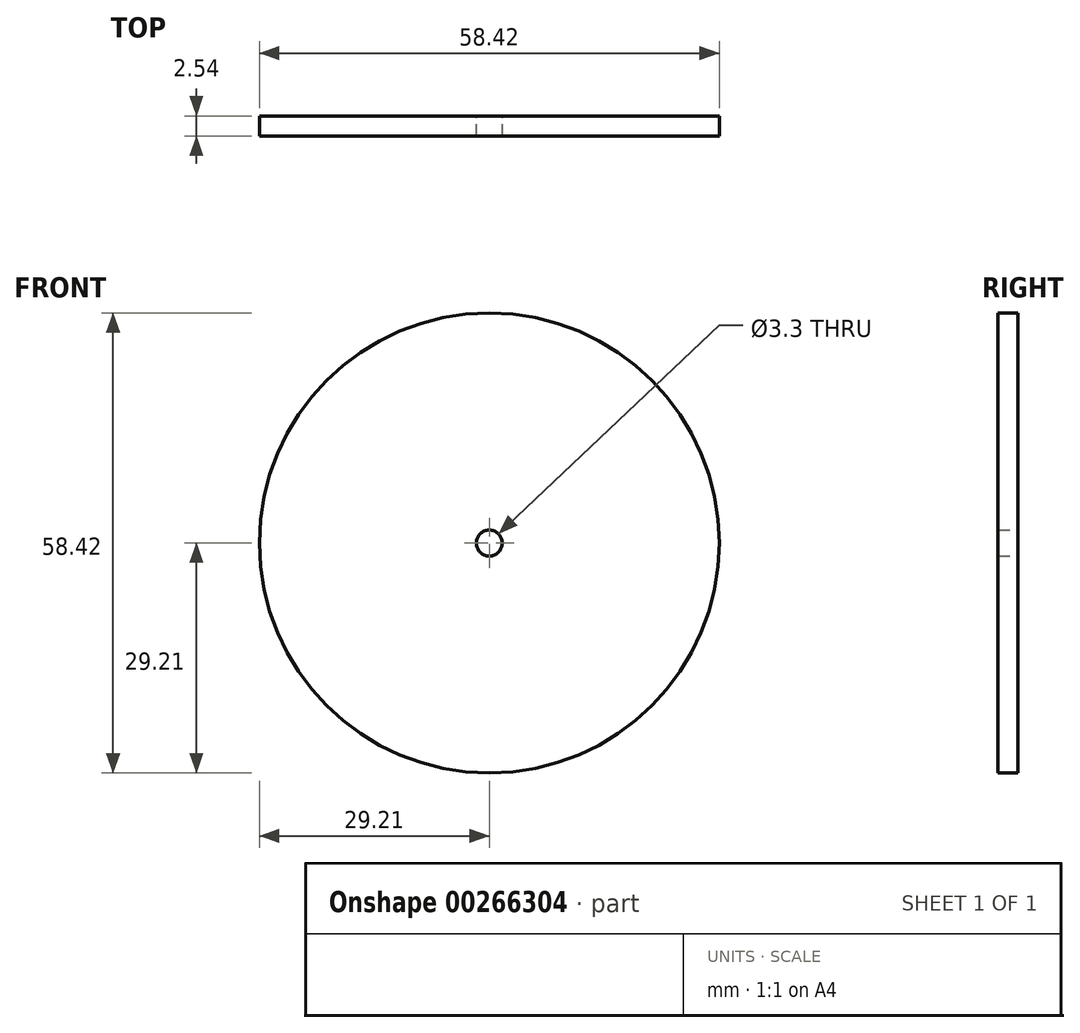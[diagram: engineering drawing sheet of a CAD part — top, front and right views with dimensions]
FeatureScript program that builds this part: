
annotation { "Feature Type Name" : "Feature", "Feature Type Description" : "" }
export const myFeature = defineFeature(function(context is Context, id is Id, definition is map)
    precondition{}
    {
        {
            var Q0;
            Q0=qCreatedBy(makeId("Front.planeOp"),FACE);
            var sketch = newSketch(context, id + "F0", { "sketchPlane" : qUnion([Q0])});
            skCircle(sketch, "E0", {"center": v(0, 0) * mm, "radius": 29.21 * mm});
            skCircle(sketch, "E1", {"center": v(0, 0) * mm, "radius": 1.65 * mm});
            skSolve(sketch);
        }
        {
            var Q0;
            Q0=makeQuery(id+"F0.imprint","IMPRINT",FACE,{"disambiguationData":[TD([[makeQuery(id+"F0.imprint","IMPRINT",EDGE,{"derivedFrom":sQuery(id+"F0.wireOp",EDGE,"E0")}),1.0]])]});
            extrude(context, id + "F1", {"entities" : qUnion([Q0]), "depth" : 2.54 * mm});
        }
    });
